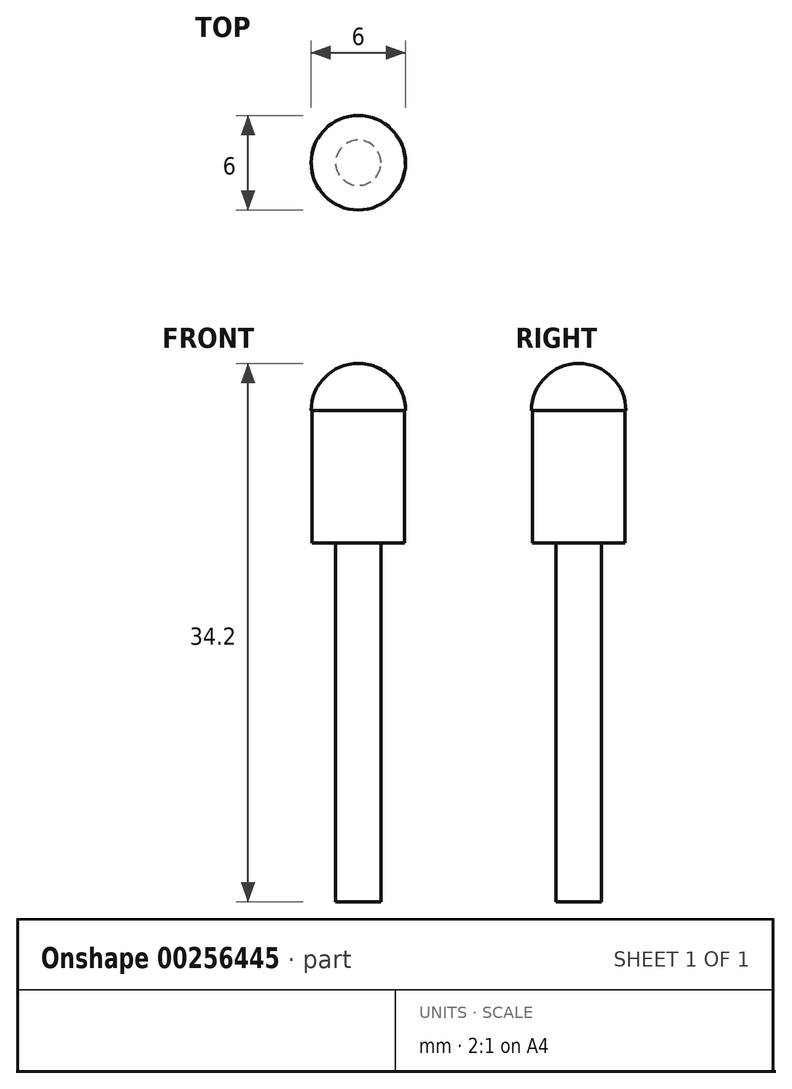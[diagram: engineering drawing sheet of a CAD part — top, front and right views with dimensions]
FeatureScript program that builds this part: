
annotation { "Feature Type Name" : "Feature", "Feature Type Description" : "" }
export const myFeature = defineFeature(function(context is Context, id is Id, definition is map)
    precondition{}
    {
        {
            var Q0;
            Q0=qCreatedBy(makeId("Top.planeOp"),FACE);
            var sketch = newSketch(context, id + "F0", { "sketchPlane" : qUnion([Q0])});
            skCircle(sketch, "E0", {"center": v(0, 0) * mm, "radius": 0.48 * mm});
            skSolve(sketch);
        }
        {
            var Q0;
            Q0=makeQuery(id+"F0.imprint","IMPRINT",FACE,{"disambiguationData":[TD([[makeQuery(id+"F0.imprint","IMPRINT",EDGE,{"derivedFrom":sQuery(id+"F0.wireOp",EDGE,"E0")}),1.0]])]});
            extrude(context, id + "F1", {"entities" : qUnion([Q0]), "depth" : 7.6 * mm});
        }
        {
            var Q0;
            Q0=makeQuery(id+"F1.opExtrude","CAP_FACE",FACE,{"disambiguationData":[OSD([sQuery(id+"F0.wireOp",EDGE,"E0")])],"isStart":false});
            var sketch = newSketch(context, id + "F2", { "sketchPlane" : qUnion([Q0])});
            skCircle(sketch, "E1", {"center": v(0, 0) * mm, "radius": 0.98 * mm});
            skSolve(sketch);
        }
        {
            var Q0;
            {var subQ0=makeQuery(id+"F2.imprint","IMPRINT",EDGE,{"derivedFrom":makeQuery(id+"F1.opExtrude","CAP_EDGE",EDGE,{"disambiguationData":[OSD([sQuery(id+"F0.wireOp",EDGE,"E0")])],"isStart":false})});Q0=qUnion([makeQuery(id+"F2.imprint","IMPRINT",FACE,{"disambiguationData":[TD([[makeQuery(id+"F2.imprint","IMPRINT",EDGE,{"derivedFrom":sQuery(id+"F2.wireOp",EDGE,"E1")}),1.0]])]}),makeQuery(id+"F2.imprint","IMPRINT",FACE,{"disambiguationData":[TD([[subQ0,1.0]])]})]);}
            extrude(context, id + "F3", {"entities" : qUnion([Q0]), "operationType" : NewBodyOperationType.ADD, "depth" : 2.8 * mm});
        }
        {
            var Q0;
            Q0=qCreatedBy(makeId("Front.planeOp"),FACE);
            var sketch = newSketch(context, id + "F4", { "sketchPlane" : qUnion([Q0])});
            skLineSegment(sketch, "E2", {"start": v(0, 0) * mm, "end": v(0, 15) * mm, "construction": true});
            skArc(sketch, "E3", {"start": v(1, 10.4) * mm, "mid": v(0.7, 11.1) * mm, "end": v(0, 11.4) * mm});
            skLineSegment(sketch, "E4", {"start": v(0, 10.4) * mm, "end": v(0, 11.4) * mm});
            skLineSegment(sketch, "E5", {"start": v(0, 10.4) * mm, "end": v(1, 10.4) * mm});
            skSolve(sketch);
        }
        {
            var Q0;
            Q0=makeQuery(id+"F4.imprint","IMPRINT",FACE,{"disambiguationData":[TD([[makeQuery(id+"F4.imprint","IMPRINT",EDGE,{"derivedFrom":sQuery(id+"F4.wireOp",EDGE,"E3")}),1.0]])]});
            var Q1;
            Q1=sQuery(id+"F4.wireOp",EDGE,"E2");
            revolve(context, id + "F5", {"operationType" : NewBodyOperationType.ADD, "entities" : qUnion([Q0]), "axis" : qUnion([Q1]), "revolveType" : RevolveType.FULL});
        }
        {
            var Q0;
            Q0=makeQuery(id+"F1.opExtrude","SWEPT_BODY",BODY,{"disambiguationData":[OSD([sQuery(id+"F0.wireOp",EDGE,"E0")])]});
            var Q1;
            Q1=qCreatedBy(makeId("Origin.pointOp"),VERTEX);
            transform(context, id + "F6", {"entities" : qUnion([Q0]), "transformType" : TransformType.SCALE_UNIFORMLY, "scale" : 3, "makeCopy" : false, "scalePoint" : qUnion([Q1])});
        }
    });
